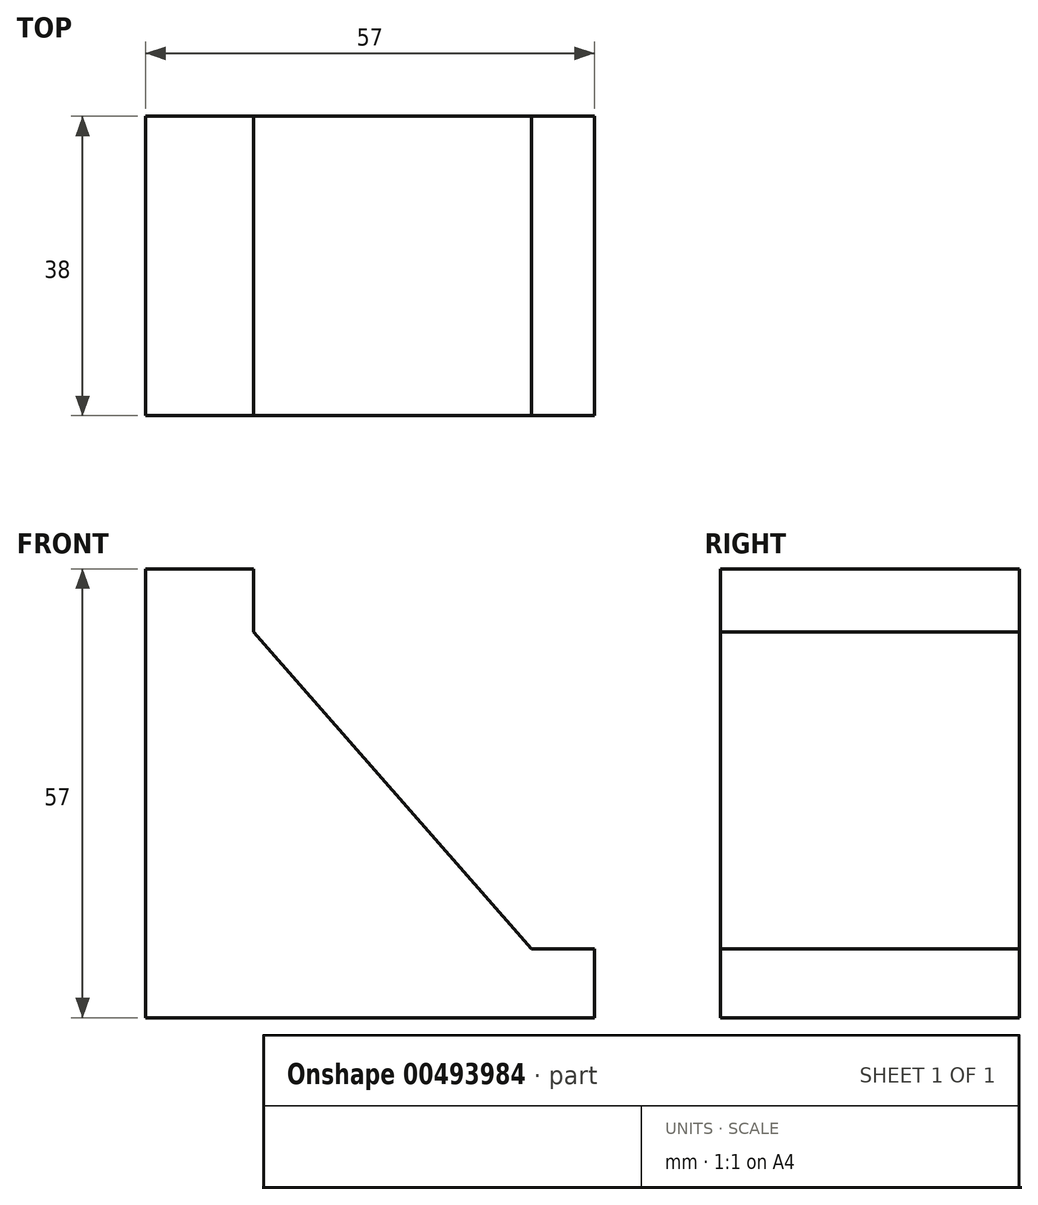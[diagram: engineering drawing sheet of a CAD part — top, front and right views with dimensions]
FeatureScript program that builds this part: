
annotation { "Feature Type Name" : "Feature", "Feature Type Description" : "" }
export const myFeature = defineFeature(function(context is Context, id is Id, definition is map)
    precondition{}
    {
        {
            var Q0;
            Q0=qCreatedBy(makeId("Front.planeOp"),FACE);
            var sketch = newSketch(context, id + "F0", { "sketchPlane" : qUnion([Q0])});
            skLineSegment(sketch, "E0", {"start": v(0, 57) * mm, "end": v(0, 0) * mm});
            skLineSegment(sketch, "E1", {"start": v(0, 0) * mm, "end": v(57, 0) * mm});
            skLineSegment(sketch, "E2", {"start": v(57, 0) * mm, "end": v(57, 8.72) * mm});
            skLineSegment(sketch, "E3", {"start": v(57, 8.72) * mm, "end": v(13.69, 8.72) * mm});
            skLineSegment(sketch, "E4", {"start": v(13.69, 8.72) * mm, "end": v(13.69, 57) * mm});
            skLineSegment(sketch, "E5", {"start": v(13.69, 57) * mm, "end": v(0, 57) * mm});
            skLineSegment(sketch, "E6", {"start": v(13.69, 49) * mm, "end": v(49, 8.72) * mm});
            skSolve(sketch);
        }
        {
            var Q0;
            {var subQ3=sQuery(id+"F0.wireOp",EDGE,"E6");Q0=makeQuery(id+"F0.imprint","IMPRINT",FACE,{"disambiguationData":[TD([[makeQuery(id+"F0.imprint","IMPRINT",EDGE,{"derivedFrom":subQ3}),-1.0]])]});}
            var Q1;
            Q1=makeQuery(id+"F0.imprint","IMPRINT",FACE,{"disambiguationData":[TD([[makeQuery(id+"F0.imprint","IMPRINT",EDGE,{"derivedFrom":sQuery(id+"F0.wireOp",EDGE,"E0")}),1.0]])]});
            extrude(context, id + "F1", {"entities" : qUnion([Q0, Q1]), "depth" : 38 * mm});
        }
    });
